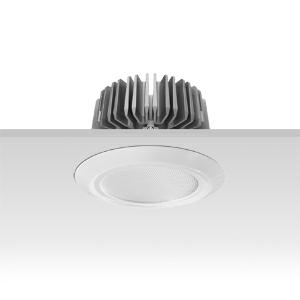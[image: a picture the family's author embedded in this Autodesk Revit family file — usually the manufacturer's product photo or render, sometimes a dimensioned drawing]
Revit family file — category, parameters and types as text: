
# Revit family: 3f_filippi_-_3f_reno_bianco_ampio_3f_filippi_-_30383_a01046_-_3f_reno_150_wh_3000-840_dali_wide___smp_wh_1c06
name_source: partatom
category: Lighting Fixtures
units: mm (PartAtom-declared; Revit-internal decimal feet)

## family parameters
Cut with Voids When Loaded = No
Host = Face
Light Source = No
Part Type = Normal
Room Calculation Point = No
Round Connector Dimension = Use Diameter
Shared = No

## types (1)
- 3F Filippi - 3F Reno Bianco Ampio (1 x LED, 2316 lm, 28 W, 4000 K)
    Apparent Load = 28 VA
    Approval mark = CE
    CIE Flux Codes = 73 92 98 100 100
    Color Rendering = 80
    Color Temperature = 4000 K
    Control Gear = Electronic transformer
    Default Elevation = 1800 mm
    Description = ILLUMINOTECHNICAL
Luminous efficiency 100% (DLOR 100%, ULOR 0%).
Initial luminous flux of the luminaire 2316 lm.
Direct symmetric wide distribution.
Installation Interdistance Transv.D = 1.01 x hu - Long.D = 1.00 x hu.
Tabular UGR (CIE 117 - 4H-8H; S=0.25H; 70/50/20): RUG 24.4 - 24.5.
Beam angle: 70° - 70°.
Luminous efficacy 83 lm/W.
Lifetime (L90/B10): 30000 h. (tq+25°C)
Lifetime (L85/B10): 50000 h. (tq+25°C)
Lifetime (L70/B10): 80000 h. (tq+25°C)
Sudden decreased luminous flux after 50000 hours: 0% (C0).
Photobiological safety in compliance with IEC/TR 62778: RG0 risk exempt, (IEC 62471).
In compliance with IEC/EN 62722-2-1 - IEC/EN 62717 standards.

SOURCE
Compact LED module 3000/840.
Energy efficiency class (UE 2019/2020 - UE 2019/2015): E.
CIE 13.3 Colour rendering index: CRI >80 (R9 <50%).
IES TM-30 Fidelity Index: Rf = 84 Rg = 95.
CCT nominal colour temperature 4000 K.
Colour initial tolerance (MacAdam): SDCM 3.
Zhaga Book 3 compliant.

MECHANICAL
Passive heat dissipator in die-casting aluminium, oversized, for optimum thermal management of the LED module.
Parabolic element with graduated/concentric rings in white polycarbonate.
Transparent external lens with glossy and satin differentiated surfaces, with a cooling and anti-insect system in methacrylate (PMMA).
Fastening spring clips in stainless steel.
Dimensions: diameter 176 mm, height 111 mm. Weight 1.34 kg.
IP44 protection degree for exposed part, IP20 for recessed part.
Mechanical strength to impacts IK05 (0.7 joule).
Glow-wire test resistance 650°C.

ELECTRICAL
Wiring on a separate unit.
Halogen Free DALI-2 DATI (Parts 251, 252, 253), PUSH-DIM, electronic wiring 230V-50/60Hz, power factor 0.97 at full load, THD <25%, constant output current, SELV, class II, 1 driver, 1 DALI addresse.
Power of the luminaire 28 W.
ENEC - CE.
SAFE FLICKER: PstLM=<1 and SVM=<0.4 (IEC TR 61547-1 and IEC TR 63158), to ensure a more comfortable and safe light.
Luminaire compliant with EN 60598-2-22 for power supply from a centralised emergency system CPSS (Central Power Supply System), not incorporated in the luminaire - high risk areas excluded. The default power and flux are 100% in AC and 100% in DC.
Ambient temperature from 0°C to +25°C.
Temperature class T6 max 85°C.
Relative humidity UR: <85%.

INSTALLATION
Pull-up recessed fitting.
False ceiling carving: 150 mm.
All accessories dedicated to this product are available on the Catalog and on our website www.3F-Filippi.com.

ACCESSORIES
A01046 - Anti-glare microprismatic SMP diffuser in methacrylate (PMMA), locked and in line with the trim, in white polycarbonate.

APPLICATIONS
Suitable product for food production plants (HACCP), IFS (Food Version 6), BRC (GSFS Food Version 7).
Environments: architectural, commercial, exhibition areas, transit areas, corridors, shops, display windows, service areas.
In false ceilings with narrow voids.

LIGHT MANAGEMENT
Recommended minimum setting: 10%.
The luminaire, equipped with (DALI-2 DATI) driver, can be controlled manually with 3F Easy Dim technology or automatically/manually with wired or wireless DALI/D2D control systems.
The D2D driver guarantees interoperability with other devices with the same certification by making the following information available:
Device Data (Part 251), Energy Report (Part 252), Diagnosis & Maintenance (Part 253).
In electrical systems without a regulation system (manual or automatic) and DALI bus, a suitable jumper must be made on the DA-DA terminals of the appliance.

WARNING
Luminaire designed for disposal/recycling at end-of-life.
Replaceable (LED only) light source by a professional. Replaceable control gear by a professional.
    Height = 0 mm  [stored 0 ft]
    Lamp = 1 x LED
    Lamp Light Flux = 2316 lm
    Lamp Power = 28 W
    Lamp count = 1
    Length = 176 mm
    Lifetime = 50000 h
    Luminous efficacy = 83 lm/W
    Manufacturer = 3F Filippi
    ModVariant = No
    Model = 3F Filippi - 30383+A01046 - 3F Reno 150 WH 3000-840 DALI WIDE + SMP WH
    Mounting Place = Ceiling
    Mounting Type = Recessed
    Number of Poles = 1
    OnlyDefault = Yes
    Power Factor = 1
    Product Name = 3F Filippi - 3F Reno Bianco Ampio
    Product group = recessed luminaire
    ProductGroupID = 4
    Protection Class = Protection class II
    Protection Degree = IP 20
    RLX_Detail_Level = 1
    RLX_Emergency_Light_Flux = 0 lm
    RLX_Emergency_Type = 0
    RLX_Emergency_Type_DB = No
    RlxData = <blob elided: 86269 chars, md5=b5228ae4>
    Socket = socket
    Standby Power = 0 W
    System Light Flux = 2316 lm
    System Power = 28 W
    Type Comments = Product without accessories
    Type Image = 3ffilippi_3f_reno_150_wh_vs_smp.jpg
    URL = http://relux.com
    VarID = ---
    Voltage = 0 V
    Weight = 0.00 kg
    Width = 0 mm  [stored 0 ft]

note: [stored X ft] marks values corroborated as IEEE doubles in the binary element streams (Revit-internal decimal feet)

## geometry (parser evidence)
native form markers: Blend x4, Sweep x12
no freeform markers — native parametric forms only
